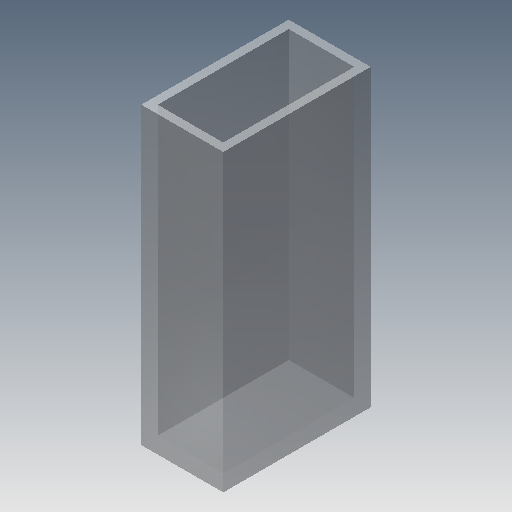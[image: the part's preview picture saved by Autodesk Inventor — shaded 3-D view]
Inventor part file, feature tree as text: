
AUTODESK INVENTOR PART (.ipt)
format: ipt  version: 2019 (Build 230136000, 136)  size: 103,936 bytes
history: native  units: mm
features: extrude x2, sketch x2
ambient origin geometry x8: Origin, YZ Plane, XZ Plane, XY Plane, X Axis, Y Axis, Z Axis, Center Point
bodies: Solid1 (feature_tree)
feature tree (4):
  extrude  "Extrusion1"  Depth=12.5mm
  extrude  "Extrusion2"  Depth=10.0mm
  sketch  "Sketch1"  dims[d0=22.5mm d1=12.5mm]
  sketch  "Sketch2"  dims[d2=45.0mm d3=0.0mm d4=10.0mm d5=20.0mm d6=1.25mm d7=1.25mm d8=43.75mm d9=0.0mm]
